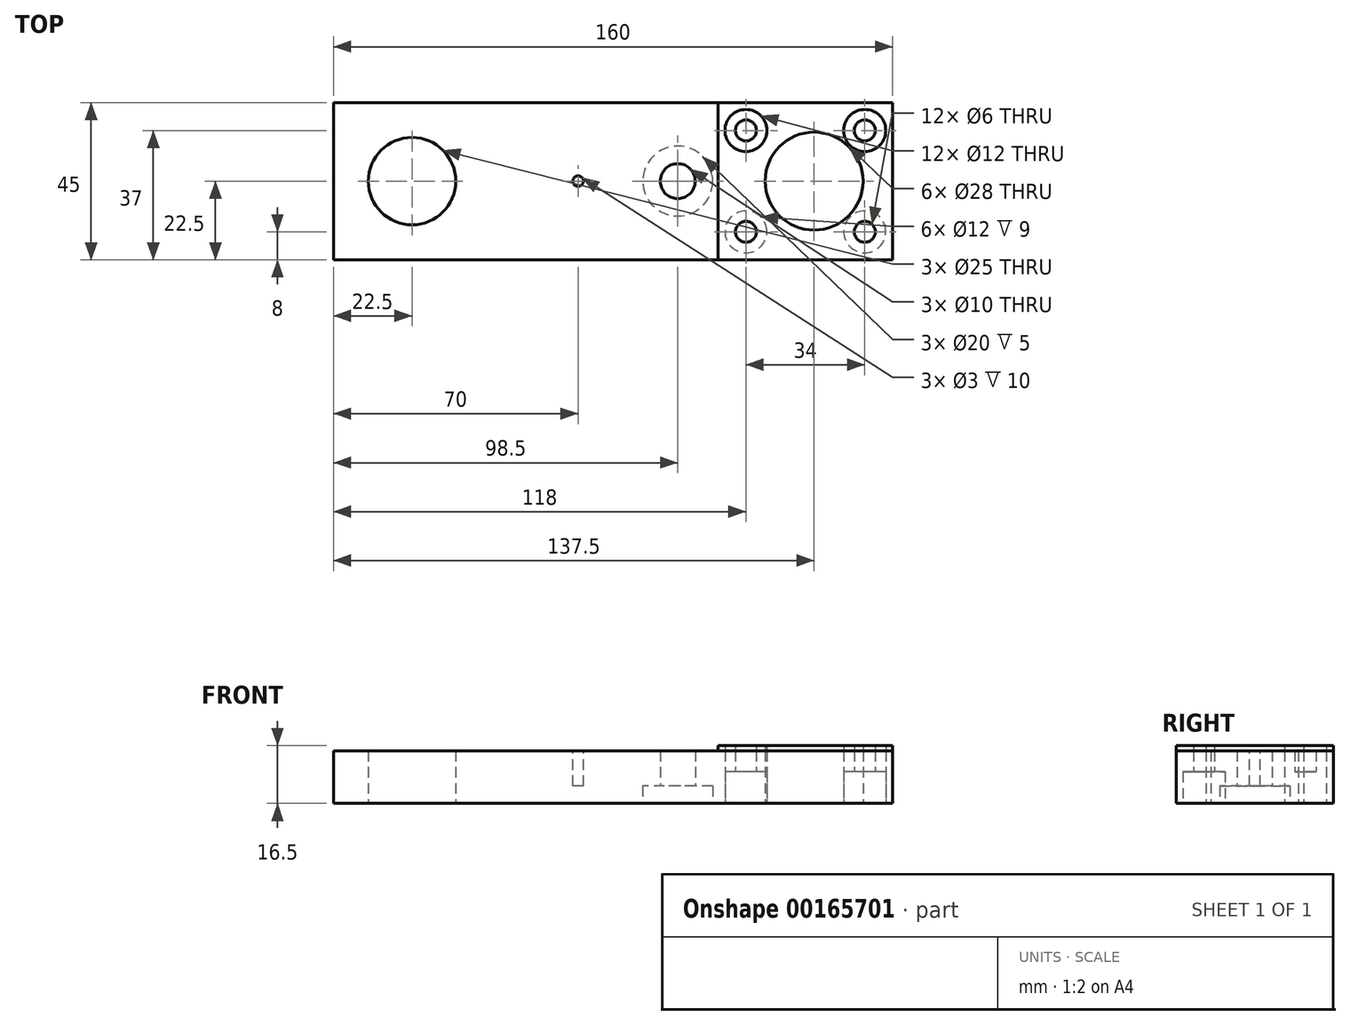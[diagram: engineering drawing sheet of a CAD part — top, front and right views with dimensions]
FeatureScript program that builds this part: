
annotation { "Feature Type Name" : "Feature", "Feature Type Description" : "" }
export const myFeature = defineFeature(function(context is Context, id is Id, definition is map)
    precondition{}
    {
        {
            var Q0;
            Q0=qCreatedBy(makeId("Top.planeOp"),FACE);
            var sketch = newSketch(context, id + "F0", { "sketchPlane" : qUnion([Q0])});
            skLineSegment(sketch, "E0.bottom", {"start": v(80, -22.5) * mm, "end": v(-80, -22.5) * mm});
            skLineSegment(sketch, "E0.top", {"start": v(80, 22.5) * mm, "end": v(-80, 22.5) * mm});
            skLineSegment(sketch, "E0.left", {"start": v(80, -22.5) * mm, "end": v(80, 22.5) * mm});
            skLineSegment(sketch, "E0.right", {"start": v(-80, -22.5) * mm, "end": v(-80, 22.5) * mm});
            skPoint(sketch, "E0.middle", {"position": v(0, 0) * mm});
            skCircle(sketch, "E1", {"center": v(57.5, 0) * mm, "radius": 14 * mm});
            skCircle(sketch, "E2", {"center": v(-57.5, 0) * mm, "radius": 12.5 * mm});
            skCircle(sketch, "E3", {"center": v(18.5, 0) * mm, "radius": 5 * mm});
            skCircle(sketch, "E4", {"center": v(72, -14.5) * mm, "radius": 3 * mm});
            skCircle(sketch, "E5", {"center": v(38, -14.5) * mm, "radius": 3 * mm});
            skCircle(sketch, "E6.MirrorC", {"center": v(38, 14.5) * mm, "radius": 3 * mm});
            skCircle(sketch, "E7.MirrorC", {"center": v(72, 14.5) * mm, "radius": 3 * mm});
            skCircle(sketch, "E8", {"center": v(18.5, 0) * mm, "radius": 10 * mm});
            skCircle(sketch, "E9", {"center": v(38, -14.5) * mm, "radius": 6 * mm});
            skCircle(sketch, "E10", {"center": v(72, -14.5) * mm, "radius": 6 * mm});
            skCircle(sketch, "E11", {"center": v(72, 14.5) * mm, "radius": 6 * mm});
            skCircle(sketch, "E12", {"center": v(38, 14.5) * mm, "radius": 6 * mm});
            skSolve(sketch);
        }
        {
            var Q0;
            Q0=makeQuery(id+"F0.imprint","IMPRINT",FACE,{"disambiguationData":[TD([[makeQuery(id+"F0.imprint","IMPRINT",EDGE,{"derivedFrom":sQuery(id+"F0.wireOp",EDGE,"E0.bottom")}),-1.0]])]});
            var Q1;
            Q1=makeQuery(id+"F0.imprint","IMPRINT",FACE,{"disambiguationData":[TD([[makeQuery(id+"F0.imprint","IMPRINT",EDGE,{"derivedFrom":sQuery(id+"F0.wireOp",EDGE,"AUW5yiXO-gH22-x4rf-6hnd-X6KtVNPjii9d")}),-1.0]])]});
            var Q2;
            Q2=makeQuery(id+"F0.imprint","IMPRINT",FACE,{"disambiguationData":[TD([[makeQuery(id+"F0.imprint","IMPRINT",EDGE,{"derivedFrom":sQuery(id+"F0.wireOp",EDGE,"E3")}),-1.0]])]});
            var Q3;
            Q3=makeQuery(id+"F0.imprint","IMPRINT",FACE,{"disambiguationData":[TD([[makeQuery(id+"F0.imprint","IMPRINT",EDGE,{"derivedFrom":sQuery(id+"F0.wireOp",EDGE,"E5")}),-1.0]])]});
            var Q4;
            Q4=makeQuery(id+"F0.imprint","IMPRINT",FACE,{"disambiguationData":[TD([[makeQuery(id+"F0.imprint","IMPRINT",EDGE,{"derivedFrom":sQuery(id+"F0.wireOp",EDGE,"E4")}),-1.0]])]});
            var Q5;
            Q5=makeQuery(id+"F0.imprint","IMPRINT",FACE,{"disambiguationData":[TD([[makeQuery(id+"F0.imprint","IMPRINT",EDGE,{"derivedFrom":sQuery(id+"F0.wireOp",EDGE,"E7.MirrorC")}),1.0]])]});
            var Q6;
            Q6=makeQuery(id+"F0.imprint","IMPRINT",FACE,{"disambiguationData":[TD([[makeQuery(id+"F0.imprint","IMPRINT",EDGE,{"derivedFrom":sQuery(id+"F0.wireOp",EDGE,"E6.MirrorC")}),1.0]])]});
            extrude(context, id + "F1", {"entities" : qUnion([Q0, Q1, Q2, Q3, Q4, Q5, Q6]), "depth" : 15 * mm, "offsetDistance" : 25 * mm});
        }
        {
            var Q0;
            Q0=makeQuery(id+"F0.imprint","IMPRINT",FACE,{"disambiguationData":[TD([[makeQuery(id+"F0.imprint","IMPRINT",EDGE,{"derivedFrom":sQuery(id+"F0.wireOp",EDGE,"AUW5yiXO-gH22-x4rf-6hnd-X6KtVNPjii9d")}),-1.0]])]});
            var Q1;
            Q1=makeQuery(id+"F0.imprint","IMPRINT",FACE,{"disambiguationData":[TD([[makeQuery(id+"F0.imprint","IMPRINT",EDGE,{"derivedFrom":sQuery(id+"F0.wireOp",EDGE,"E3")}),-1.0]])]});
            extrude(context, id + "F2", {"entities" : qUnion([Q0, Q1]), "operationType" : NewBodyOperationType.REMOVE, "depth" : 5 * mm, "offsetDistance" : 25 * mm});
        }
        {
            var Q0;
            Q0=makeQuery(id+"F0.imprint","IMPRINT",FACE,{"disambiguationData":[TD([[makeQuery(id+"F0.imprint","IMPRINT",EDGE,{"derivedFrom":sQuery(id+"F0.wireOp",EDGE,"E5")}),-1.0]])]});
            var Q1;
            Q1=makeQuery(id+"F0.imprint","IMPRINT",FACE,{"disambiguationData":[TD([[makeQuery(id+"F0.imprint","IMPRINT",EDGE,{"derivedFrom":sQuery(id+"F0.wireOp",EDGE,"E4")}),-1.0]])]});
            var Q2;
            Q2=makeQuery(id+"F0.imprint","IMPRINT",FACE,{"disambiguationData":[TD([[makeQuery(id+"F0.imprint","IMPRINT",EDGE,{"derivedFrom":sQuery(id+"F0.wireOp",EDGE,"E7.MirrorC")}),1.0]])]});
            var Q3;
            Q3=makeQuery(id+"F0.imprint","IMPRINT",FACE,{"disambiguationData":[TD([[makeQuery(id+"F0.imprint","IMPRINT",EDGE,{"derivedFrom":sQuery(id+"F0.wireOp",EDGE,"E6.MirrorC")}),1.0]])]});
            extrude(context, id + "F3", {"entities" : qUnion([Q0, Q1, Q2, Q3]), "operationType" : NewBodyOperationType.REMOVE, "depth" : 9 * mm, "offsetDistance" : 25 * mm});
        }
        {
            var Q0;
            Q0=makeQuery(id+"F1.opExtrude","CAP_FACE",FACE,{"disambiguationData":[OSD([sQuery(id+"F0.wireOp",EDGE,"E0.bottom"),sQuery(id+"F0.wireOp",EDGE,"E0.top"),sQuery(id+"F0.wireOp",EDGE,"E0.left"),sQuery(id+"F0.wireOp",EDGE,"E0.right"),sQuery(id+"F0.wireOp",EDGE,"E1"),sQuery(id+"F0.wireOp",EDGE,"E2"),sQuery(id+"F0.wireOp",EDGE,"AUW5yiXO-gH22-x4rf-6hnd-X6KtVNPjii9d"),sQuery(id+"F0.wireOp",EDGE,"E3"),sQuery(id+"F0.wireOp",EDGE,"E4"),sQuery(id+"F0.wireOp",EDGE,"E5"),sQuery(id+"F0.wireOp",EDGE,"E6.MirrorC"),sQuery(id+"F0.wireOp",EDGE,"E7.MirrorC")])],"isStart":false});
            var sketch = newSketch(context, id + "F4", { "sketchPlane" : qUnion([Q0])});
            skCircle(sketch, "E13", {"center": v(-10, 0) * mm, "radius": 1.5 * mm});
            skSolve(sketch);
        }
        {
            var Q0;
            Q0=makeQuery(id+"F4.imprint","IMPRINT",FACE,{"disambiguationData":[TD([[makeQuery(id+"F4.imprint","IMPRINT",EDGE,{"derivedFrom":sQuery(id+"F4.wireOp",EDGE,"E13")}),1.0]])]});
            extrude(context, id + "F5", {"entities" : qUnion([Q0]), "operationType" : NewBodyOperationType.REMOVE, "oppositeDirection" : true, "depth" : 10 * mm, "offsetDistance" : 25 * mm});
        }
        {
            var Q0;
            Q0=makeQuery(id+"F1.opExtrude","CAP_FACE",FACE,{"disambiguationData":[OSD([sQuery(id+"F0.wireOp",EDGE,"E0.bottom"),sQuery(id+"F0.wireOp",EDGE,"E0.top"),sQuery(id+"F0.wireOp",EDGE,"E0.left"),sQuery(id+"F0.wireOp",EDGE,"E0.right"),sQuery(id+"F0.wireOp",EDGE,"E1"),sQuery(id+"F0.wireOp",EDGE,"E2"),sQuery(id+"F0.wireOp",EDGE,"AUW5yiXO-gH22-x4rf-6hnd-X6KtVNPjii9d"),sQuery(id+"F0.wireOp",EDGE,"E3"),sQuery(id+"F0.wireOp",EDGE,"E4"),sQuery(id+"F0.wireOp",EDGE,"E5"),sQuery(id+"F0.wireOp",EDGE,"E6.MirrorC"),sQuery(id+"F0.wireOp",EDGE,"E7.MirrorC")])],"isStart":false});
            var sketch = newSketch(context, id + "F6", { "sketchPlane" : qUnion([Q0])});
            skLineSegment(sketch, "E14.bottom", {"start": v(80, 22.5) * mm, "end": v(30, 22.5) * mm});
            skLineSegment(sketch, "E14.top", {"start": v(80, -22.5) * mm, "end": v(30, -22.5) * mm});
            skLineSegment(sketch, "E14.left", {"start": v(80, 22.5) * mm, "end": v(80, -22.5) * mm});
            skLineSegment(sketch, "E14.right", {"start": v(30, 22.5) * mm, "end": v(30, -22.5) * mm});
            skSolve(sketch);
        }
        {
            var Q0;
            Q0=makeQuery(id+"F6.imprint","IMPRINT",FACE,{"disambiguationData":[TD([[makeQuery(id+"F6.imprint","IMPRINT",EDGE,{"derivedFrom":sQuery(id+"F6.wireOp",EDGE,"E14.bottom")}),1.0]])]});
            extrude(context, id + "F7", {"entities" : qUnion([Q0]), "depth" : 1.5 * mm, "offsetDistance" : 25 * mm});
        }
    });
